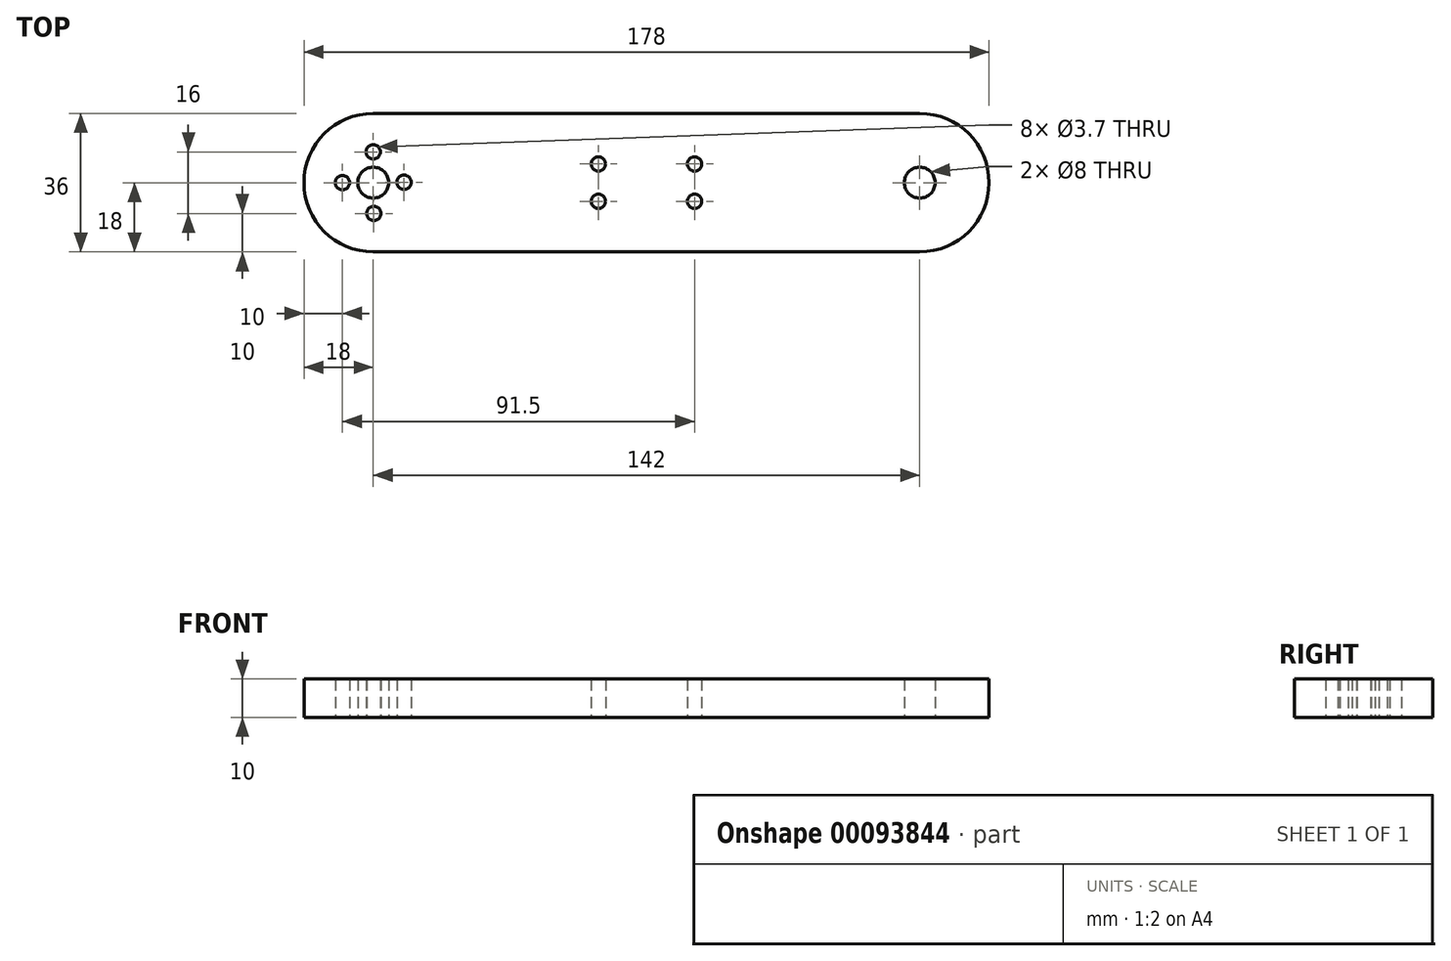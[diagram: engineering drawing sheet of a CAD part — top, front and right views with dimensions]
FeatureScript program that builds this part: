
annotation { "Feature Type Name" : "Feature", "Feature Type Description" : "" }
export const myFeature = defineFeature(function(context is Context, id is Id, definition is map)
    precondition{}
    {
        {
            var Q0;
            Q0=qCreatedBy(makeId("Top.planeOp"),FACE);
            var sketch = newSketch(context, id + "F0", { "sketchPlane" : qUnion([Q0])});
            skArc(sketch, "E0", {"start": v(71, -18) * mm, "mid": v(89, 0) * mm, "end": v(71, 18) * mm});
            skArc(sketch, "E1", {"start": v(-71, 18) * mm, "mid": v(-89, 0) * mm, "end": v(-71, -18) * mm});
            skCircle(sketch, "E2", {"center": v(-71, 0) * mm, "radius": 4 * mm});
            skCircle(sketch, "E3", {"center": v(12.5, -4.85) * mm, "radius": 1.85 * mm});
            skCircle(sketch, "E4", {"center": v(12.5, 4.85) * mm, "radius": 1.85 * mm});
            skCircle(sketch, "E5", {"center": v(-12.5, 4.85) * mm, "radius": 1.85 * mm});
            skCircle(sketch, "E6", {"center": v(-12.5, -4.85) * mm, "radius": 1.85 * mm});
            skCircle(sketch, "E7", {"center": v(71, 0) * mm, "radius": 4 * mm});
            skLineSegment(sketch, "E8", {"start": v(71, 0) * mm, "end": v(71, 4) * mm});
            skLineSegment(sketch, "E9", {"start": v(71, 18) * mm, "end": v(-71, 18) * mm});
            skLineSegment(sketch, "E10", {"start": v(-71, -18) * mm, "end": v(71, -18) * mm});
            skCircle(sketch, "E11", {"center": v(-79, 0) * mm, "radius": 1.85 * mm});
            skCircle(sketch, "E12", {"center": v(-71, 8) * mm, "radius": 1.85 * mm});
            skCircle(sketch, "E13", {"center": v(-70.84, -8) * mm, "radius": 1.85 * mm});
            skCircle(sketch, "E14", {"center": v(-63, 0.1) * mm, "radius": 1.85 * mm});
            skSolve(sketch);
        }
        {
            var Q0;
            Q0=makeQuery(id+"F0.imprint","IMPRINT",FACE,{"disambiguationData":[TD([[makeQuery(id+"F0.imprint","IMPRINT",EDGE,{"derivedFrom":sQuery(id+"F0.wireOp",EDGE,"E0")}),1.0]])]});
            extrude(context, id + "F1", {"entities" : qUnion([Q0]), "depth" : 10 * mm});
        }
    });
